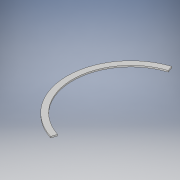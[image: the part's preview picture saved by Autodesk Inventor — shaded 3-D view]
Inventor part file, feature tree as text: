
AUTODESK INVENTOR PART (.ipt)
format: ipt  version: 2017 (Build 210142000, 142)  size: 108,544 bytes
history: native  units: in
note: dims shown in document units (in); Inventor stores cm internally (conversion verified against a paired STEP export)
features: extrude x1, sketch x1
ambient origin geometry x8: Origin, YZ Plane, XZ Plane, XY Plane, X Axis, Y Axis, Z Axis, Center Point
bodies: Solid1 (feature_tree)
feature tree (2):
  extrude  "Extrusion1"  Depth=5.2in
  sketch  "Sketch1"  dims[d0=5.2in d1=5.2in d2=5.2in d3=5.2in d4=5.2in d13=11.4in d15=0.4947in d17=0.125in d18=0.0in]
